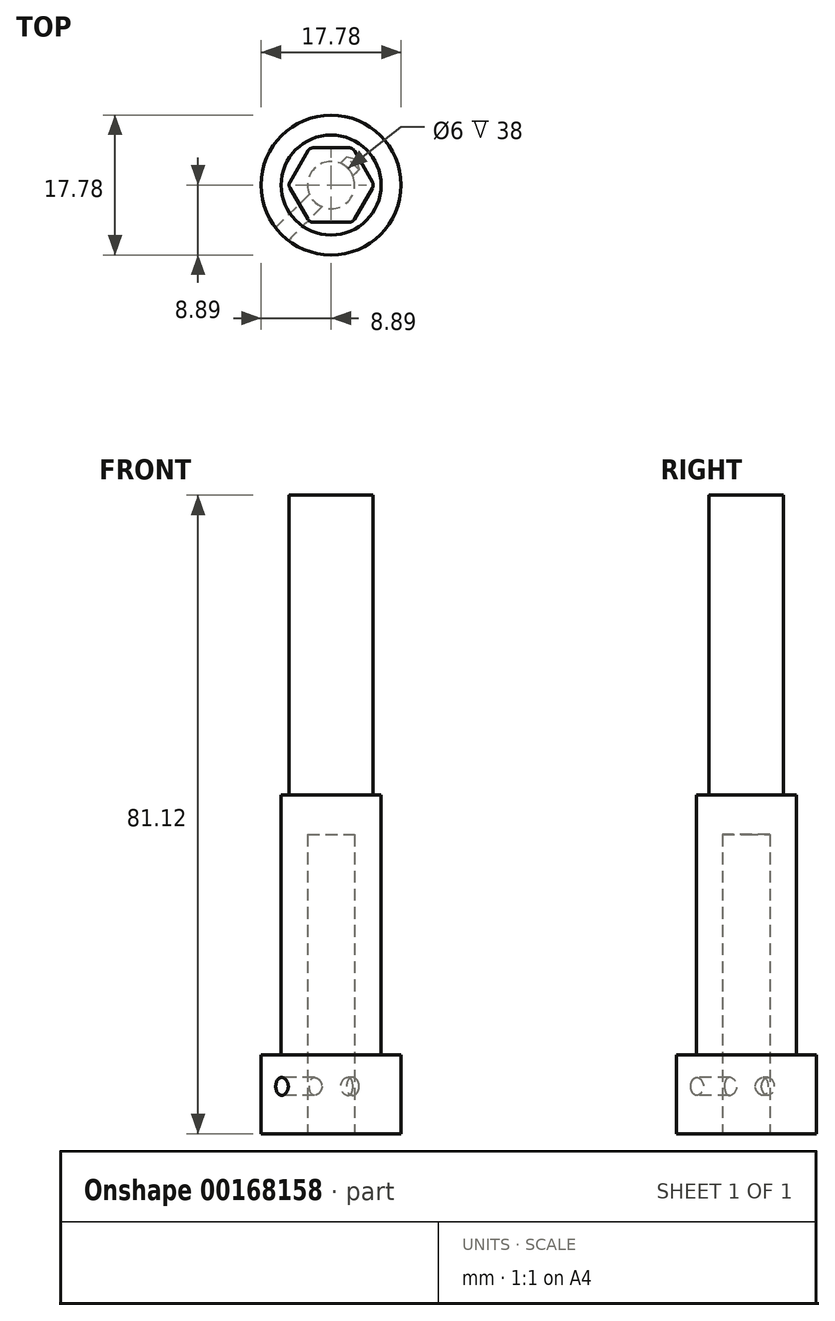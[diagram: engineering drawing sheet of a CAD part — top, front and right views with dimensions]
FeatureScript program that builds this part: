
annotation { "Feature Type Name" : "Feature", "Feature Type Description" : "" }
export const myFeature = defineFeature(function(context is Context, id is Id, definition is map)
    precondition{}
    {
        {
            var Q0;
            Q0=qCreatedBy(makeId("Top.planeOp"),FACE);
            var sketch = newSketch(context, id + "F0", { "sketchPlane" : qUnion([Q0])});
            skCircle(sketch, "E0", {"center": v(0, 0) * mm, "radius": 8.9 * mm});
            skSolve(sketch);
        }
        {
            var Q0;
            Q0=makeQuery(id+"F0.imprint","IMPRINT",FACE,{"disambiguationData":[TD([[makeQuery(id+"F0.imprint","IMPRINT",EDGE,{"derivedFrom":sQuery(id+"F0.wireOp",EDGE,"E0")}),1.0]])]});
            extrude(context, id + "F1", {"entities" : qUnion([Q0]), "depth" : 10 * mm});
        }
        {
            var Q0;
            Q0=makeQuery(id+"F1.opExtrude","CAP_FACE",FACE,{"disambiguationData":[OSD([sQuery(id+"F0.wireOp",EDGE,"E0")])],"isStart":false});
            var sketch = newSketch(context, id + "F2", { "sketchPlane" : qUnion([Q0])});
            skCircle(sketch, "E1", {"center": v(0, 0) * mm, "radius": 6.35 * mm});
            skSolve(sketch);
        }
        {
            var Q0;
            Q0=qSketchRegion(id+"F2",true);
            extrude(context, id + "F3", {"entities" : qUnion([Q0]), "operationType" : NewBodyOperationType.ADD, "depth" : 33.02 * mm});
        }
        {
            var Q0;
            Q0=makeQuery(id+"F3.opExtrude","CAP_FACE",FACE,{"disambiguationData":[OSD([sQuery(id+"F2.wireOp",EDGE,"E1")])],"isStart":false});
            var sketch = newSketch(context, id + "F4", { "sketchPlane" : qUnion([Q0])});
            skCircle(sketch, "E2.cCircle", {"center": v(0, 0) * mm, "radius": 4.72 * mm, "construction": true});
            skLineSegment(sketch, "E2.0", {"start": v(5.46, 0) * mm, "end": v(2.73, -4.72) * mm});
            skLineSegment(sketch, "E2.1", {"start": v(2.73, -4.72) * mm, "end": v(-2.73, -4.72) * mm});
            skLineSegment(sketch, "E2.2", {"start": v(-2.73, -4.72) * mm, "end": v(-5.46, 0) * mm});
            skLineSegment(sketch, "E2.3", {"start": v(-5.46, 0) * mm, "end": v(-2.73, 4.72) * mm});
            skLineSegment(sketch, "E2.4", {"start": v(-2.73, 4.72) * mm, "end": v(2.73, 4.72) * mm});
            skLineSegment(sketch, "E2.5", {"start": v(2.73, 4.72) * mm, "end": v(5.46, 0) * mm});
            skPoint(sketch, "E2.0.midPoint", {"position": v(4.1, -2.36) * mm});
            skSolve(sketch);
        }
        {
            var Q0;
            Q0=makeQuery(id+"F4.imprint","IMPRINT",FACE,{"disambiguationData":[TD([[makeQuery(id+"F4.imprint","IMPRINT",EDGE,{"derivedFrom":sQuery(id+"F4.wireOp",EDGE,"E2.0")}),-1.0]])]});
            extrude(context, id + "F5", {"entities" : qUnion([Q0]), "operationType" : NewBodyOperationType.ADD, "depth" : 38.1 * mm});
        }
        {
            var Q0;
            Q0=makeQuery(id+"F5.opExtrude","SWEPT_EDGE",EDGE,{"disambiguationData":[OSD([sQuery(id+"F4.wireOp",EDGE,"E2.1"),sQuery(id+"F4.wireOp",EDGE,"E2.2")])]});
            var Q1;
            Q1=makeQuery(id+"F5.opExtrude","SWEPT_EDGE",EDGE,{"disambiguationData":[OSD([sQuery(id+"F4.wireOp",EDGE,"E2.0"),sQuery(id+"F4.wireOp",EDGE,"E2.1")])]});
            var Q2;
            Q2=makeQuery(id+"F5.opExtrude","SWEPT_EDGE",EDGE,{"disambiguationData":[OSD([sQuery(id+"F4.wireOp",EDGE,"E2.0"),sQuery(id+"F4.wireOp",EDGE,"E2.5")])]});
            var Q3;
            Q3=makeQuery(id+"F5.opExtrude","SWEPT_EDGE",EDGE,{"disambiguationData":[OSD([sQuery(id+"F4.wireOp",EDGE,"E2.4"),sQuery(id+"F4.wireOp",EDGE,"E2.5")])]});
            var Q4;
            Q4=makeQuery(id+"F5.opExtrude","SWEPT_EDGE",EDGE,{"disambiguationData":[OSD([sQuery(id+"F4.wireOp",EDGE,"E2.3"),sQuery(id+"F4.wireOp",EDGE,"E2.4")])]});
            var Q5;
            Q5=makeQuery(id+"F5.opExtrude","SWEPT_EDGE",EDGE,{"disambiguationData":[OSD([sQuery(id+"F4.wireOp",EDGE,"E2.2"),sQuery(id+"F4.wireOp",EDGE,"E2.3")])]});
            fillet(context, id + "F6", {"entities" : qUnion([Q0, Q1, Q2, Q3, Q4, Q5]), "radius" : 0.76 * mm, "tangentPropagation" : true, "allowEdgeOverflow" : false});
        }
        {
            var Q0;
            Q0=makeQuery(id+"F1.opExtrude","CAP_FACE",FACE,{"disambiguationData":[OSD([sQuery(id+"F0.wireOp",EDGE,"E0")])],"isStart":true});
            var sketch = newSketch(context, id + "F7", { "sketchPlane" : qUnion([Q0])});
            skCircle(sketch, "E3", {"center": v(0, 0) * mm, "radius": 3 * mm});
            skSolve(sketch);
        }
        {
            var Q0;
            Q0=qSketchRegion(id+"F7",true);
            extrude(context, id + "F8", {"entities" : qUnion([Q0]), "operationType" : NewBodyOperationType.REMOVE, "oppositeDirection" : true, "depth" : 38 * mm});
        }
        {
            var Q0;
            Q0=qCreatedBy(makeId("Front.planeOp"),FACE);
            var sketch = newSketch(context, id + "F9", { "sketchPlane" : qUnion([Q0])});
            skLineSegment(sketch, "E4", {"start": v(0, 0) * mm, "end": v(0, 37.16) * mm, "construction": true});
            skSolve(sketch);
        }
        {
            var Q0;
            Q0=sQuery(id+"F9.wireOp",EDGE,"E4");
            cPlane(context, id + "F10", {"entities" : qUnion([Q0]), "cplaneType" : CPlaneType.LINE_ANGLE, "offset" : 25.4 * mm, "angle" : 45 * degree, "width" : 152.4 * mm, "height" : 152.4 * mm});
        }
        {
            var Q0;
            Q0=makeQuery(id+"F1.opExtrude","CAP_FACE",FACE,{"disambiguationData":[OSD([sQuery(id+"F0.wireOp",EDGE,"E0")])],"isStart":false});
            var sketch = newSketch(context, id + "F11", { "sketchPlane" : qUnion([Q0])});
            skCircle(sketch, "E5.0", {"center": v(0, 0) * mm, "radius": 8.9 * mm, "construction": true});
            skLineSegment(sketch, "E6", {"start": v(0, 0) * mm, "end": v(-6.29, -6.29) * mm, "construction": true});
            skSolve(sketch);
        }
        {
            var Q0;
            Q0=qCreatedBy(id+"F10.planeOp",FACE);
            var Q1;
            Q1=sQuery(id+"F11.wireOp",VERTEX,"E6.end");
            cPlane(context, id + "F12", {"entities" : qUnion([Q0, Q1]), "cplaneType" : CPlaneType.PLANE_POINT, "offset" : 25.4 * mm, "width" : 152.4 * mm, "height" : 152.4 * mm});
        }
        {
            var Q0;
            Q0=qCreatedBy(id+"F12.planeOp",FACE);
            var sketch = newSketch(context, id + "F13", { "sketchPlane" : qUnion([Q0])});
            skLineSegment(sketch, "E7", {"start": v(0, 10) * mm, "end": v(0, 6) * mm, "construction": true});
            skPoint(sketch, "E8", {"position": v(0, 6) * mm});
            skSolve(sketch);
        }
        {
            var Q0;
            Q0=sQuery(id+"F13.wireOp",VERTEX,"E8");
            var Q1;
            Q1=makeQuery(id+"F1.opExtrude","SWEPT_BODY",BODY,{"disambiguationData":[OSD([sQuery(id+"F0.wireOp",EDGE,"E0")])]});
            hole(context, id + "F14", {"style" : HoleStyle.SIMPLE, "endStyle" : HoleEndStyle.BLIND, "oppositeDirection" : true, "standardTappedOrClearance" : lookupTablePath({ "standard" : "ANSI", "engagement" : "75%", "pitch" : "40 tpi", "size" : "#4", "type" : "Tapped" }), "standardBlindInLast" : lookupTablePath({ "standard" : "ANSI", "engagement" : "75%", "pitch" : "40 tpi", "size" : "#4", "type" : "Tapped" }), "holeDiameter" : 2.26 * mm, "holeDepth" : 12.7 * mm, "locations" : qUnion([Q0]), "scope" : qUnion([Q1]), "majorDiameter" : 2.84 * mm});
        }
    });
